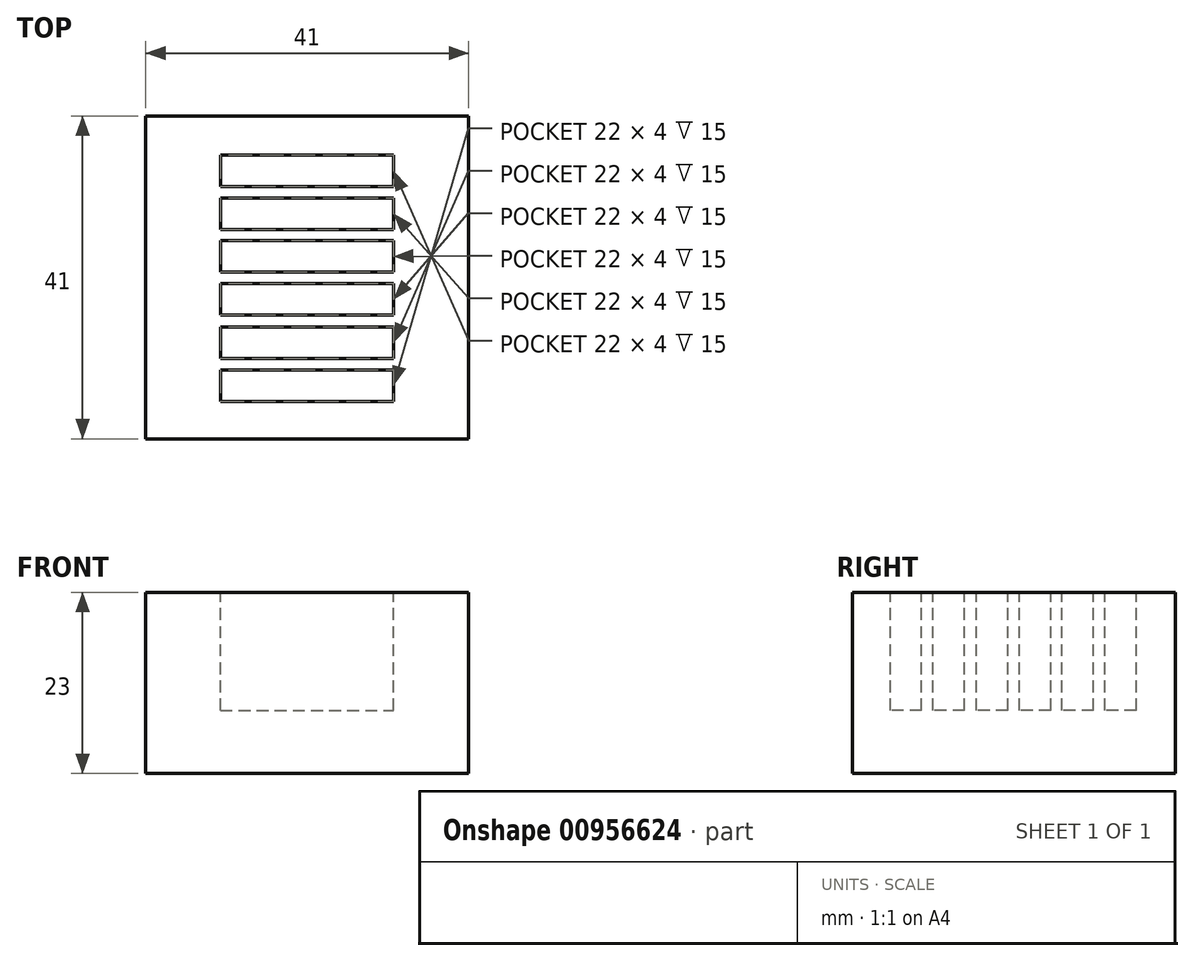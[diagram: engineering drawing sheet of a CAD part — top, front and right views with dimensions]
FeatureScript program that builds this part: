
annotation { "Feature Type Name" : "Feature", "Feature Type Description" : "" }
export const myFeature = defineFeature(function(context is Context, id is Id, definition is map)
    precondition{}
    {
        {
            var Q0;
            Q0=qCreatedBy(makeId("Top.planeOp"),FACE);
            var sketch = newSketch(context, id + "F0", { "sketchPlane" : qUnion([Q0])});
            skLineSegment(sketch, "E0.bottom", {"start": v(-20.5, 20.5) * mm, "end": v(20.5, 20.5) * mm});
            skLineSegment(sketch, "E0.top", {"start": v(-20.5, -20.5) * mm, "end": v(20.5, -20.5) * mm});
            skLineSegment(sketch, "E0.left", {"start": v(-20.5, 20.5) * mm, "end": v(-20.5, -20.5) * mm});
            skLineSegment(sketch, "E0.right", {"start": v(20.5, 20.5) * mm, "end": v(20.5, -20.5) * mm});
            skPoint(sketch, "E0.middle", {"position": v(0, 0) * mm});
            skSolve(sketch);
        }
        {
            var Q0;
            Q0=makeQuery(id+"F0.imprint","IMPRINT",FACE,{"disambiguationData":[TD([[makeQuery(id+"F0.imprint","IMPRINT",EDGE,{"derivedFrom":sQuery(id+"F0.wireOp",EDGE,"E0.bottom")}),-1.0]])]});
            extrude(context, id + "F1", {"entities" : qUnion([Q0]), "depth" : 23 * mm, "offsetDistance" : 25 * mm});
        }
        {
            var Q0;
            Q0=makeQuery(id+"F1.opExtrude","CAP_FACE",FACE,{"disambiguationData":[OSD([sQuery(id+"F0.wireOp",EDGE,"E0.bottom"),sQuery(id+"F0.wireOp",EDGE,"E0.top"),sQuery(id+"F0.wireOp",EDGE,"E0.left"),sQuery(id+"F0.wireOp",EDGE,"E0.right")])],"isStart":false});
            var sketch = newSketch(context, id + "F2", { "sketchPlane" : qUnion([Q0])});
            skLineSegment(sketch, "E1.bottom", {"start": v(-11, 15.54) * mm, "end": v(11, 15.54) * mm});
            skLineSegment(sketch, "E1.top", {"start": v(-11, 11.54) * mm, "end": v(11, 11.54) * mm});
            skLineSegment(sketch, "E1.left", {"start": v(-11, 15.54) * mm, "end": v(-11, 11.54) * mm});
            skLineSegment(sketch, "E1.right", {"start": v(11, 15.54) * mm, "end": v(11, 11.54) * mm});
            skPoint(sketch, "E1.middle", {"position": v(0, 13.54) * mm});
            skLineSegment(sketch, "E2.bottom", {"start": v(-11, 10.1) * mm, "end": v(11, 10.1) * mm});
            skLineSegment(sketch, "E2.top", {"start": v(-11, 6.1) * mm, "end": v(11, 6.1) * mm});
            skLineSegment(sketch, "E2.left", {"start": v(-11, 10.1) * mm, "end": v(-11, 6.1) * mm});
            skLineSegment(sketch, "E2.right", {"start": v(11, 10.1) * mm, "end": v(11, 6.1) * mm});
            skLineSegment(sketch, "E3.bottom", {"start": v(-11, 4.68) * mm, "end": v(11, 4.68) * mm});
            skLineSegment(sketch, "E3.top", {"start": v(-11, 0.68) * mm, "end": v(11, 0.68) * mm});
            skLineSegment(sketch, "E3.left", {"start": v(-11, 4.68) * mm, "end": v(-11, 0.68) * mm});
            skLineSegment(sketch, "E3.right", {"start": v(11, 4.68) * mm, "end": v(11, 0.68) * mm});
            skLineSegment(sketch, "E4.bottom", {"start": v(-11, -0.77) * mm, "end": v(11, -0.77) * mm});
            skLineSegment(sketch, "E4.top", {"start": v(-11, -4.77) * mm, "end": v(11, -4.77) * mm});
            skLineSegment(sketch, "E4.left", {"start": v(-11, -0.77) * mm, "end": v(-11, -4.77) * mm});
            skLineSegment(sketch, "E4.right", {"start": v(11, -0.77) * mm, "end": v(11, -4.77) * mm});
            skLineSegment(sketch, "E5.bottom", {"start": v(-11, -6.28) * mm, "end": v(11, -6.28) * mm});
            skLineSegment(sketch, "E5.top", {"start": v(-11, -10.28) * mm, "end": v(11, -10.28) * mm});
            skLineSegment(sketch, "E5.left", {"start": v(-11, -6.28) * mm, "end": v(-11, -10.28) * mm});
            skLineSegment(sketch, "E5.right", {"start": v(11, -6.28) * mm, "end": v(11, -10.28) * mm});
            skLineSegment(sketch, "E6.bottom", {"start": v(-11, -11.73) * mm, "end": v(11, -11.73) * mm});
            skLineSegment(sketch, "E6.top", {"start": v(-11, -15.73) * mm, "end": v(11, -15.73) * mm});
            skLineSegment(sketch, "E6.left", {"start": v(-11, -11.73) * mm, "end": v(-11, -15.73) * mm});
            skLineSegment(sketch, "E6.right", {"start": v(11, -11.73) * mm, "end": v(11, -15.73) * mm});
            skSolve(sketch);
        }
        {
            var Q0;
            Q0 = qSketchRegion(id + "F2", true);
            extrude(context, id + "F3", {"entities" : qUnion([Q0]), "operationType" : NewBodyOperationType.REMOVE, "oppositeDirection" : true, "depth" : 15 * mm, "offsetDistance" : 25 * mm});
        }
    });
